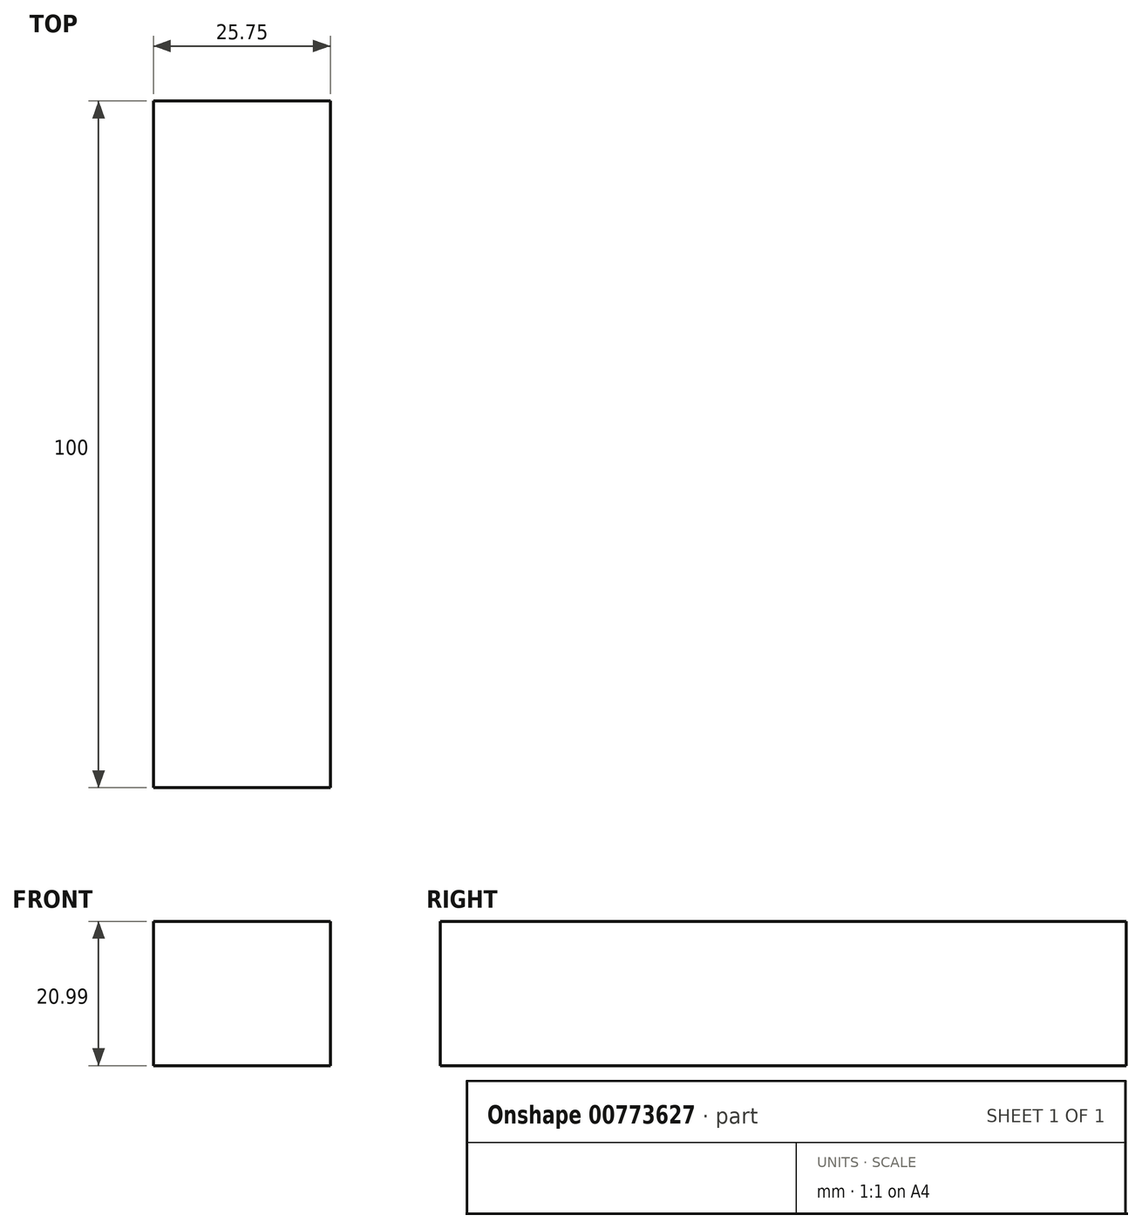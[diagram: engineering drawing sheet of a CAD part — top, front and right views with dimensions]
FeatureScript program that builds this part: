
annotation { "Feature Type Name" : "Feature", "Feature Type Description" : "" }
export const myFeature = defineFeature(function(context is Context, id is Id, definition is map)
    precondition{}
    {
        {
            var Q0;
            Q0=qCreatedBy(makeId("Front.planeOp"),FACE);
            var sketch = newSketch(context, id + "F0", { "sketchPlane" : qUnion([Q0])});
            skLineSegment(sketch, "E0.bottom", {"start": v(0, 0) * mm, "end": v(25.75, 0) * mm});
            skLineSegment(sketch, "E0.top", {"start": v(0, -20.99) * mm, "end": v(25.75, -20.99) * mm});
            skLineSegment(sketch, "E0.left", {"start": v(0, 0) * mm, "end": v(0, -20.99) * mm});
            skLineSegment(sketch, "E0.right", {"start": v(25.75, 0) * mm, "end": v(25.75, -20.99) * mm});
            skPoint(sketch, "E1.oppositeSnap0", {"position": v(12.87, 0) * mm});
            skLineSegment(sketch, "E1.bottom", {"start": v(25.75, -10.5) * mm, "end": v(52.57, -10.5) * mm});
            skLineSegment(sketch, "E1.top", {"start": v(25.75, 0) * mm, "end": v(52.57, 0) * mm});
            skLineSegment(sketch, "E1.left", {"start": v(25.75, -10.5) * mm, "end": v(25.75, 0) * mm});
            skLineSegment(sketch, "E1.right", {"start": v(52.57, -10.5) * mm, "end": v(52.57, 0) * mm});
            skLineSegment(sketch, "E2.bottom", {"start": v(52.57, 0) * mm, "end": v(75.07, 0) * mm});
            skLineSegment(sketch, "E2.top", {"start": v(52.57, -23.87) * mm, "end": v(75.07, -23.87) * mm});
            skLineSegment(sketch, "E2.left", {"start": v(52.57, 0) * mm, "end": v(52.57, -23.87) * mm});
            skLineSegment(sketch, "E2.right", {"start": v(75.07, 0) * mm, "end": v(75.07, -23.87) * mm});
            skSolve(sketch);
        }
        {
            var Q0;
            Q0=makeQuery(id+"F0.imprint","IMPRINT",FACE,{"disambiguationData":[TD([[makeQuery(id+"F0.imprint","IMPRINT",EDGE,{"derivedFrom":sQuery(id+"F0.wireOp",EDGE,"E0.bottom")}),-1.0]])]});
            extrude(context, id + "F1", {"entities" : qUnion([Q0]), "depth" : 100 * mm, "offsetDistance" : 25 * mm});
        }
    });
